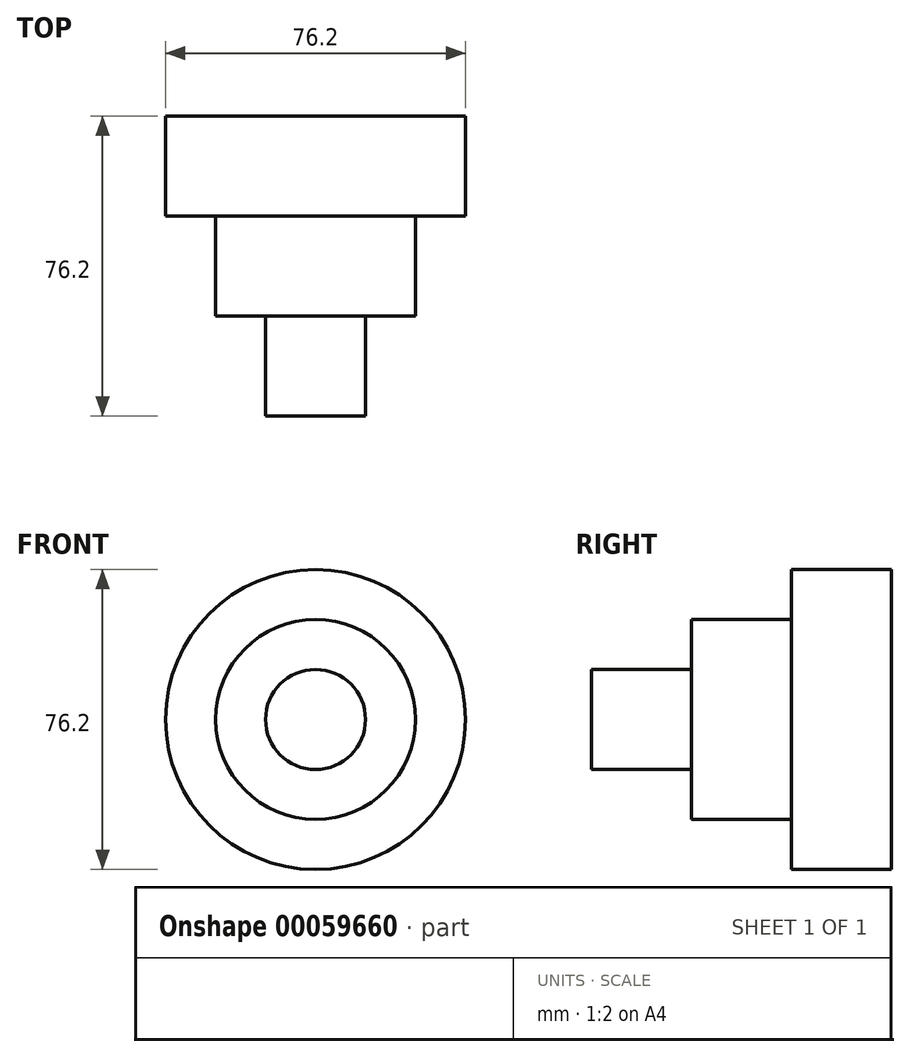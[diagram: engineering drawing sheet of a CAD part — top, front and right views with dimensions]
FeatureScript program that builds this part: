
annotation { "Feature Type Name" : "Feature", "Feature Type Description" : "" }
export const myFeature = defineFeature(function(context is Context, id is Id, definition is map)
    precondition{}
    {
        {
            var Q0;
            Q0=qCreatedBy(makeId("Front.planeOp"),FACE);
            var sketch = newSketch(context, id + "F0", { "sketchPlane" : qUnion([Q0])});
            skCircle(sketch, "E0", {"center": v(0, 0) * mm, "radius": 38.1 * mm});
            skSolve(sketch);
        }
        {
            var Q0;
            Q0 = qSketchRegion(id + "F0", true);
            extrude(context, id + "F1", {"entities" : qUnion([Q0]), "depth" : 76.2 * mm});
        }
        {
            var Q0;
            Q0=qCreatedBy(makeId("Top.planeOp"),FACE);
            var sketch = newSketch(context, id + "F2", { "sketchPlane" : qUnion([Q0])});
            skLineSegment(sketch, "E1", {"start": v(-12.7, -76.2) * mm, "end": v(-12.7, -50.8) * mm});
            skLineSegment(sketch, "E2", {"start": v(-12.7, -50.8) * mm, "end": v(-25.4, -50.8) * mm});
            skLineSegment(sketch, "E3", {"start": v(-25.4, -50.8) * mm, "end": v(-25.4, -25.4) * mm});
            skLineSegment(sketch, "E4", {"start": v(-25.4, -25.4) * mm, "end": v(-50.8, -25.4) * mm});
            skLineSegment(sketch, "E5", {"start": v(-50.8, -25.4) * mm, "end": v(-50.8, -76.2) * mm});
            skLineSegment(sketch, "E6", {"start": v(-50.8, -76.2) * mm, "end": v(-12.7, -76.2) * mm});
            skLineSegment(sketch, "E7", {"start": v(0, 0) * mm, "end": v(0, -26.63) * mm, "construction": true});
            skSolve(sketch);
        }
        {
            var Q0;
            Q0 = qSketchRegion(id + "F2", true);
            var Q1;
            Q1=sQuery(id+"F2.wireOp",EDGE,"E7");
            revolve(context, id + "F3", {"operationType" : NewBodyOperationType.REMOVE, "entities" : qUnion([Q0]), "axis" : qUnion([Q1]), "revolveType" : RevolveType.FULL, "oppositeDirection" : true});
        }
    });
